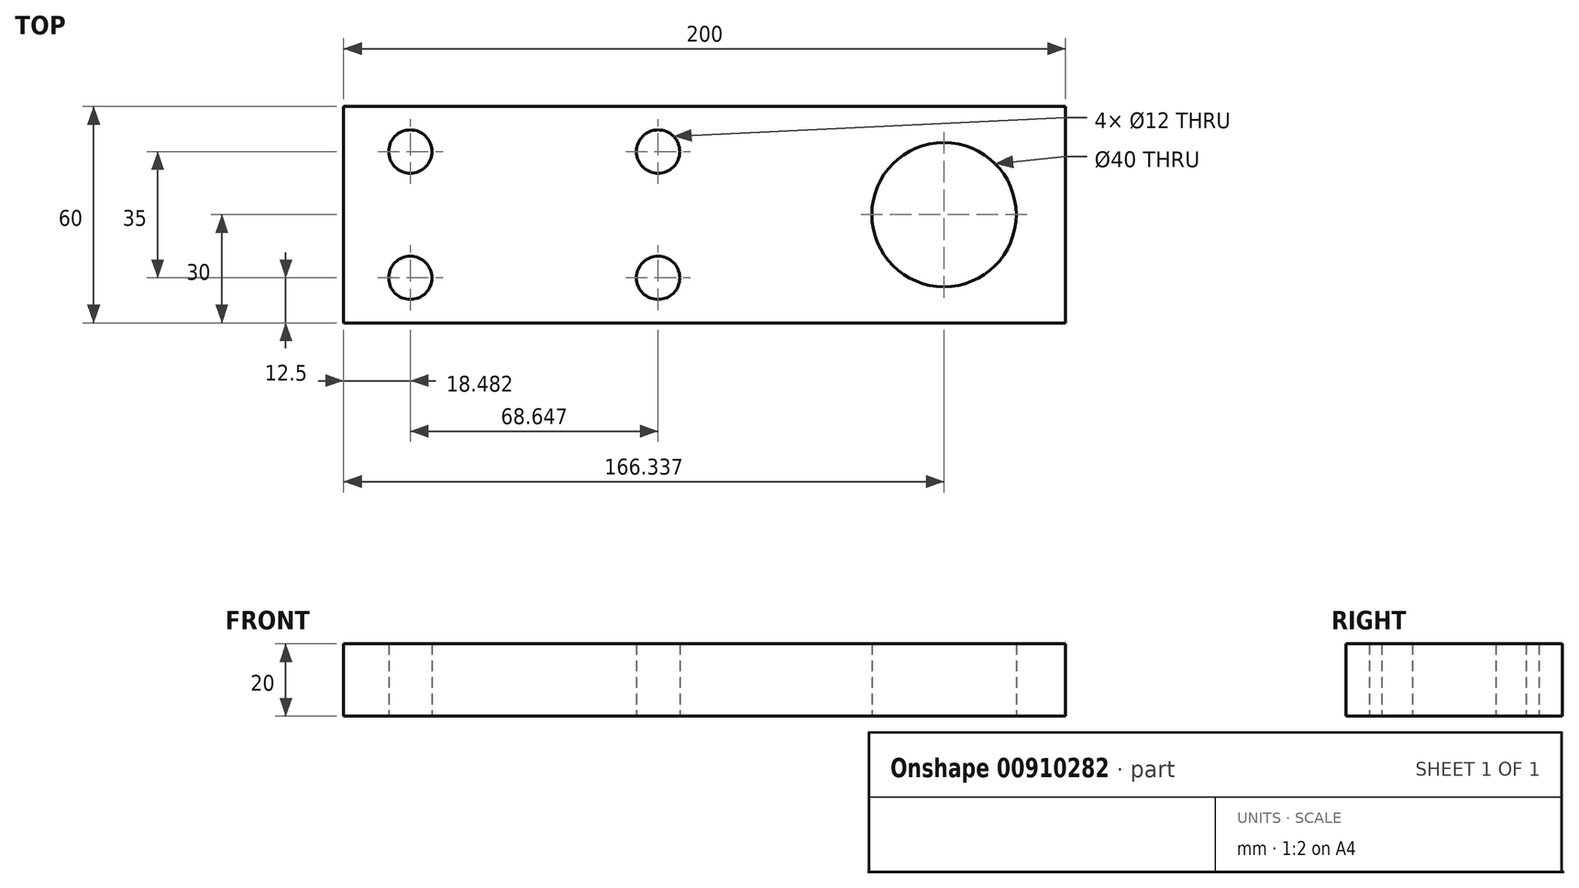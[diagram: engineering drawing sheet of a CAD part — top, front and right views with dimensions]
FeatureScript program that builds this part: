
annotation { "Feature Type Name" : "Feature", "Feature Type Description" : "" }
export const myFeature = defineFeature(function(context is Context, id is Id, definition is map)
    precondition{}
    {
        {
            var Q0;
            Q0=qCreatedBy(makeId("Top.planeOp"),FACE);
            var sketch = newSketch(context, id + "F0", { "sketchPlane" : qUnion([Q0])});
            skLineSegment(sketch, "E0.bottom", {"start": v(-100, 30) * mm, "end": v(100, 30) * mm});
            skLineSegment(sketch, "E0.top", {"start": v(-100, -30) * mm, "end": v(100, -30) * mm});
            skLineSegment(sketch, "E0.left", {"start": v(-100, 30) * mm, "end": v(-100, -30) * mm});
            skLineSegment(sketch, "E0.right", {"start": v(100, 30) * mm, "end": v(100, -30) * mm});
            skPoint(sketch, "E0.middle", {"position": v(0, 0) * mm});
            skCircle(sketch, "E1", {"center": v(66.34, 0) * mm, "radius": 20 * mm});
            skCircle(sketch, "E2", {"center": v(-12.87, 17.5) * mm, "radius": 6 * mm});
            skCircle(sketch, "E3", {"center": v(-81.52, 17.5) * mm, "radius": 6 * mm});
            skCircle(sketch, "E4", {"center": v(-12.87, -17.5) * mm, "radius": 6 * mm});
            skCircle(sketch, "E5", {"center": v(-81.52, -17.5) * mm, "radius": 6 * mm});
            skLineSegment(sketch, "E6", {"start": v(-81.52, 17.5) * mm, "end": v(-81.52, 0) * mm, "construction": true});
            skLineSegment(sketch, "E7", {"start": v(-81.52, 0) * mm, "end": v(-81.52, -17.5) * mm, "construction": true});
            skSolve(sketch);
        }
        {
            var Q0;
            Q0=makeQuery(id+"F0.imprint","IMPRINT",FACE,{"disambiguationData":[TD([[makeQuery(id+"F0.imprint","IMPRINT",EDGE,{"derivedFrom":sQuery(id+"F0.wireOp",EDGE,"E0.bottom")}),-1.0]])]});
            extrude(context, id + "F1", {"entities" : qUnion([Q0]), "depth" : 20 * mm, "offsetDistance" : 25 * mm});
        }
    });
